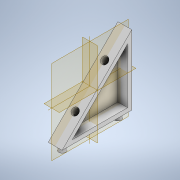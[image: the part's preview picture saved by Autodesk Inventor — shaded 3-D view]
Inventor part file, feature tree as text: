
AUTODESK INVENTOR PART (.ipt)
format: ipt  version: 2022.4 (Build 264492010, 492A)  size: 140,800 bytes
history: native  units: mm
features: extrude x4, sketch x4
ambient origin geometry x8: Origin, YZ Plane, XZ Plane, XY Plane, X Axis, Y Axis, Z Axis, Center Point
bodies: Solid1 (feature_tree)
feature tree (8):
  extrude  "Extrusion1"  Depth=50.0mm
  extrude  "Extrusion2"  Depth=3.0mm
  extrude  "Extrusion3"  Depth=5.0mm
  extrude  "Extrusion4"  Depth=10.0mm
  sketch  "Sketch2"  dims[d0=50.0mm d1=50.0mm]
  sketch  "Sketch4"  dims[d2=10.0mm d3=0.0mm d8=3.0mm]
  sketch  "Sketch5"  dims[d9=7.0mm d10=0.0mm d11=5.0mm]
  sketch  "Sketch8"  dims[d12=5.0mm d13=20.0mm d15=40.0mm d16=10.0mm d18=10.0mm d20=5.0mm d21=0.0mm d31=70.710678mm d32=5.0mm d34=15.0mm d35=7.0mm d36=0.0mm]
